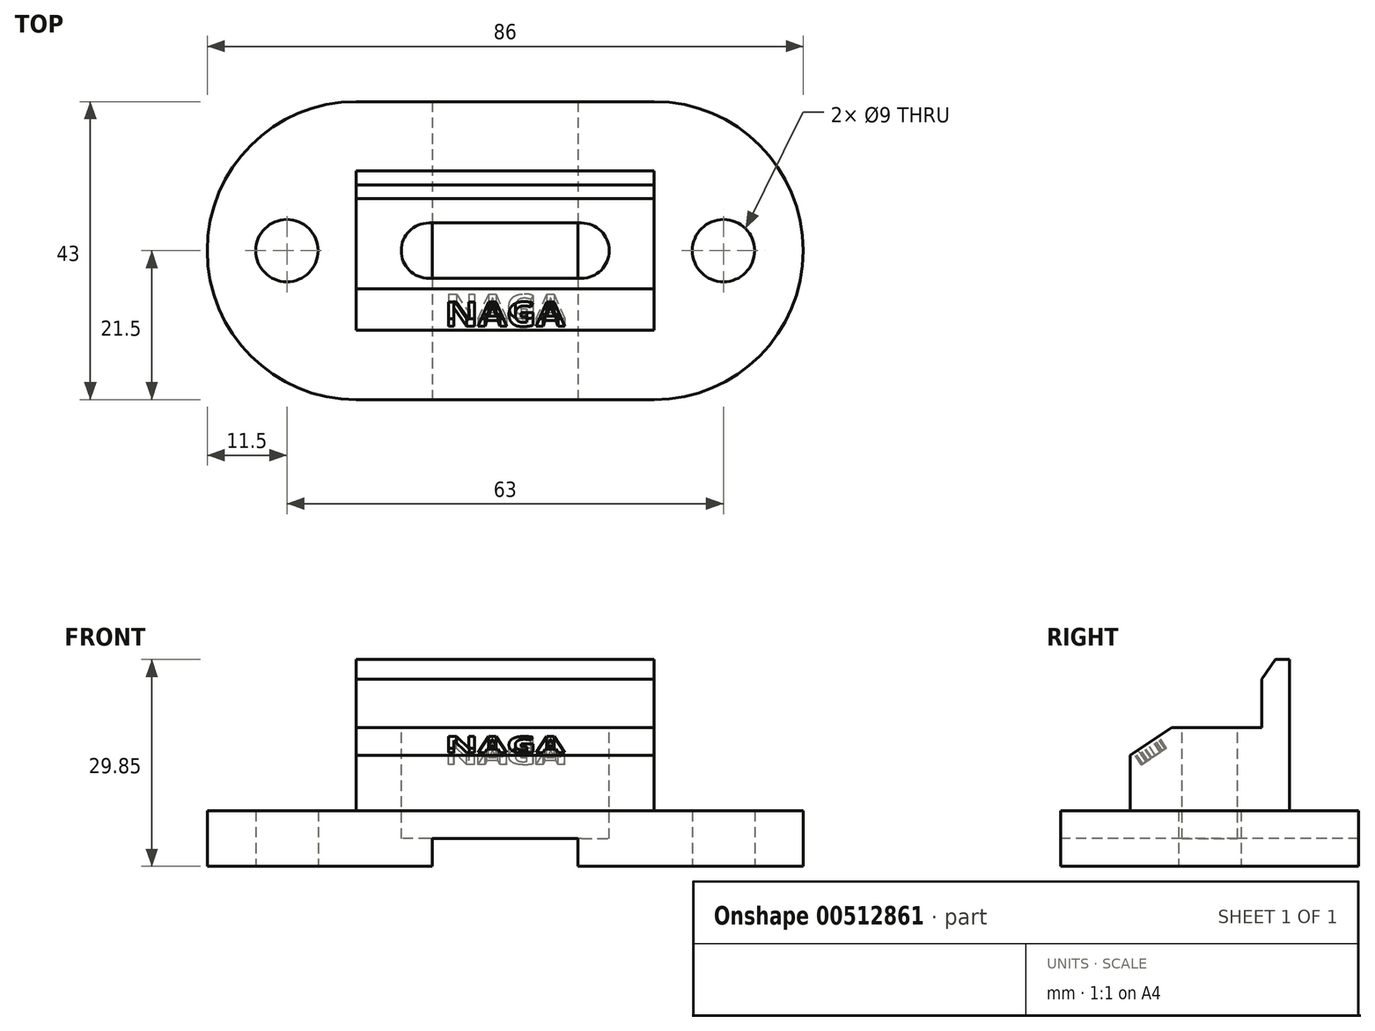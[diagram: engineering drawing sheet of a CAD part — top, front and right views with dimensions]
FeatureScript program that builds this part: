
annotation { "Feature Type Name" : "Feature", "Feature Type Description" : "" }
export const myFeature = defineFeature(function(context is Context, id is Id, definition is map)
    precondition{}
    {
        {
            var Q0;
            Q0=qCreatedBy(makeId("Top.planeOp"),FACE);
            var sketch = newSketch(context, id + "F0", { "sketchPlane" : qUnion([Q0])});
            skLineSegment(sketch, "E0.bottom", {"start": v(21.5, -21.5) * mm, "end": v(-21.5, -21.5) * mm});
            skLineSegment(sketch, "E0.top", {"start": v(21.5, 21.5) * mm, "end": v(-21.5, 21.5) * mm});
            skLineSegment(sketch, "E0.left", {"start": v(21.5, -21.5) * mm, "end": v(21.5, 21.5) * mm});
            skLineSegment(sketch, "E0.right", {"start": v(-21.5, -21.5) * mm, "end": v(-21.5, 21.5) * mm});
            skPoint(sketch, "E0.middle", {"position": v(0, 0) * mm});
            skArc(sketch, "E1", {"start": v(-21.5, 21.5) * mm, "mid": v(-43, 0) * mm, "end": v(-21.5, -21.5) * mm});
            skArc(sketch, "E2", {"start": v(21.5, -21.5) * mm, "mid": v(43, 0) * mm, "end": v(21.5, 21.5) * mm});
            skLineSegment(sketch, "E3", {"start": v(0, -9.05) * mm, "end": v(0, 9.23) * mm, "construction": true});
            skCircle(sketch, "E4", {"center": v(31.5, 0) * mm, "radius": 4.5 * mm});
            skCircle(sketch, "E5.MirrorC", {"center": v(-31.5, 0) * mm, "radius": 4.5 * mm});
            skSolve(sketch);
        }
        {
            var Q0;
            Q0 = qSketchRegion(id + "F0", true);
            extrude(context, id + "F1", {"entities" : qUnion([Q0]), "depth" : 8 * mm});
        }
        {
            var Q0;
            Q0=makeQuery(id+"F1.opExtrude","SWEPT_FACE",FACE,{"disambiguationData":[OSD([sQuery(id+"F0.wireOp",EDGE,"E0.bottom")])]});
            var sketch = newSketch(context, id + "F2", { "sketchPlane" : qUnion([Q0])});
            skLineSegment(sketch, "E6.bottom", {"start": v(-10.5, 0) * mm, "end": v(10.5, 0) * mm});
            skLineSegment(sketch, "E6.top", {"start": v(-10.5, 4) * mm, "end": v(10.5, 4) * mm});
            skLineSegment(sketch, "E6.left", {"start": v(-10.5, 0) * mm, "end": v(-10.5, 4) * mm});
            skLineSegment(sketch, "E6.right", {"start": v(10.5, 0) * mm, "end": v(10.5, 4) * mm});
            skSolve(sketch);
        }
        {
            var Q0;
            Q0 = qSketchRegion(id + "F2", true);
            extrude(context, id + "F3", {"entities" : qUnion([Q0]), "operationType" : NewBodyOperationType.REMOVE, "oppositeDirection" : true, "depth" : 43 * mm});
        }
        {
            var Q0;
            Q0=makeQuery(id+"F1.opExtrude","CAP_FACE",FACE,{"disambiguationData":[OSD([sQuery(id+"F0.wireOp",EDGE,"E0.bottom"),sQuery(id+"F0.wireOp",EDGE,"E0.top"),sQuery(id+"F0.wireOp",EDGE,"E1"),sQuery(id+"F0.wireOp",EDGE,"E2"),sQuery(id+"F0.wireOp",EDGE,"E4"),sQuery(id+"F0.wireOp",EDGE,"E5.MirrorC")])],"isStart":false});
            var sketch = newSketch(context, id + "F4", { "sketchPlane" : qUnion([Q0])});
            skLineSegment(sketch, "E7.0", {"start": v(21.5, -21.5) * mm, "end": v(21.5, 21.5) * mm});
            skLineSegment(sketch, "E8.0", {"start": v(-21.5, -21.5) * mm, "end": v(-21.5, 21.5) * mm});
            skLineSegment(sketch, "E9.bottom", {"start": v(-21.5, -11.5) * mm, "end": v(21.5, -11.5) * mm});
            skLineSegment(sketch, "E9.top", {"start": v(-21.5, 11.5) * mm, "end": v(21.5, 11.5) * mm});
            skLineSegment(sketch, "E9.left", {"start": v(-21.5, -11.5) * mm, "end": v(-21.5, 11.5) * mm});
            skLineSegment(sketch, "E9.right", {"start": v(21.5, -11.5) * mm, "end": v(21.5, 11.5) * mm});
            skSolve(sketch);
        }
        {
            var Q0;
            Q0=qCreatedBy(makeId("Right.planeOp"),FACE);
            var sketch = newSketch(context, id + "F5", { "sketchPlane" : qUnion([Q0])});
            skLineSegment(sketch, "E10", {"start": v(-11.5, 8) * mm, "end": v(-11.5, 16) * mm});
            skLineSegment(sketch, "E11", {"start": v(-11.5, 16) * mm, "end": v(-5.5, 20) * mm});
            skLineSegment(sketch, "E12", {"start": v(-5.5, 20) * mm, "end": v(7.5, 20) * mm});
            skLineSegment(sketch, "E13", {"start": v(7.5, 20) * mm, "end": v(7.5, 27) * mm});
            skLineSegment(sketch, "E14", {"start": v(7.5, 27) * mm, "end": v(9.5, 29.85) * mm});
            skLineSegment(sketch, "E15", {"start": v(9.5, 29.85) * mm, "end": v(11.5, 29.85) * mm});
            skLineSegment(sketch, "E16", {"start": v(11.5, 29.85) * mm, "end": v(11.5, 8) * mm});
            skLineSegment(sketch, "E17", {"start": v(11.5, 8) * mm, "end": v(-11.5, 8) * mm});
            skSolve(sketch);
        }
        {
            var Q0;
            Q0 = qSketchRegion(id + "F5", true);
            extrude(context, id + "F6", {"entities" : qUnion([Q0]), "operationType" : NewBodyOperationType.ADD, "endBound" : BoundingType.SYMMETRIC, "depth" : 43 * mm});
        }
        {
            var Q0;
            Q0=makeQuery(id+"F6.opExtrude","SWEPT_FACE",FACE,{"disambiguationData":[OSD([sQuery(id+"F5.wireOp",EDGE,"E12")])]});
            var sketch = newSketch(context, id + "F7", { "sketchPlane" : qUnion([Q0])});
            skLineSegment(sketch, "E18.bottom", {"start": v(11, -4) * mm, "end": v(-11, -4) * mm});
            skLineSegment(sketch, "E18.top", {"start": v(11, 4) * mm, "end": v(-11, 4) * mm});
            skLineSegment(sketch, "E18.left", {"start": v(11, -4) * mm, "end": v(11, 4) * mm});
            skLineSegment(sketch, "E18.right", {"start": v(-11, -4) * mm, "end": v(-11, 4) * mm});
            skPoint(sketch, "E18.middle", {"position": v(0, 0) * mm});
            skArc(sketch, "E19", {"start": v(11, -4) * mm, "mid": v(15, 0) * mm, "end": v(11, 4) * mm});
            skArc(sketch, "E20", {"start": v(-11, 4) * mm, "mid": v(-15, 0) * mm, "end": v(-11, -4) * mm});
            skSolve(sketch);
        }
        {
            var Q0;
            Q0 = qSketchRegion(id + "F7", true);
            extrude(context, id + "F8", {"entities" : qUnion([Q0]), "operationType" : NewBodyOperationType.REMOVE, "oppositeDirection" : true, "depth" : 16 * mm});
        }
        {
            var Q0;
            Q0=makeQuery(id+"F6.opExtrude","SWEPT_FACE",FACE,{"disambiguationData":[OSD([sQuery(id+"F5.wireOp",EDGE,"E11")])]});
            var sketch = newSketch(context, id + "F9", { "sketchPlane" : qUnion([Q0])});
            skText(sketch, "E21", { "text": "NAGA", "fontName": "OpenSans-Bold.ttf"});
            const initialGuessF9  = {"E21": [-0.00872, 0, 1, 0, 0.00427]};
            skSetInitialGuess(sketch, initialGuessF9);
            skSolve(sketch);
        }
        {
            var Q0;
            Q0 = qSketchRegion(id + "F9", true);
            extrude(context, id + "F10", {"entities" : qUnion([Q0]), "operationType" : NewBodyOperationType.REMOVE, "oppositeDirection" : true, "depth" : 2 * mm, "offsetDistance" : 25 * mm});
        }
    });
